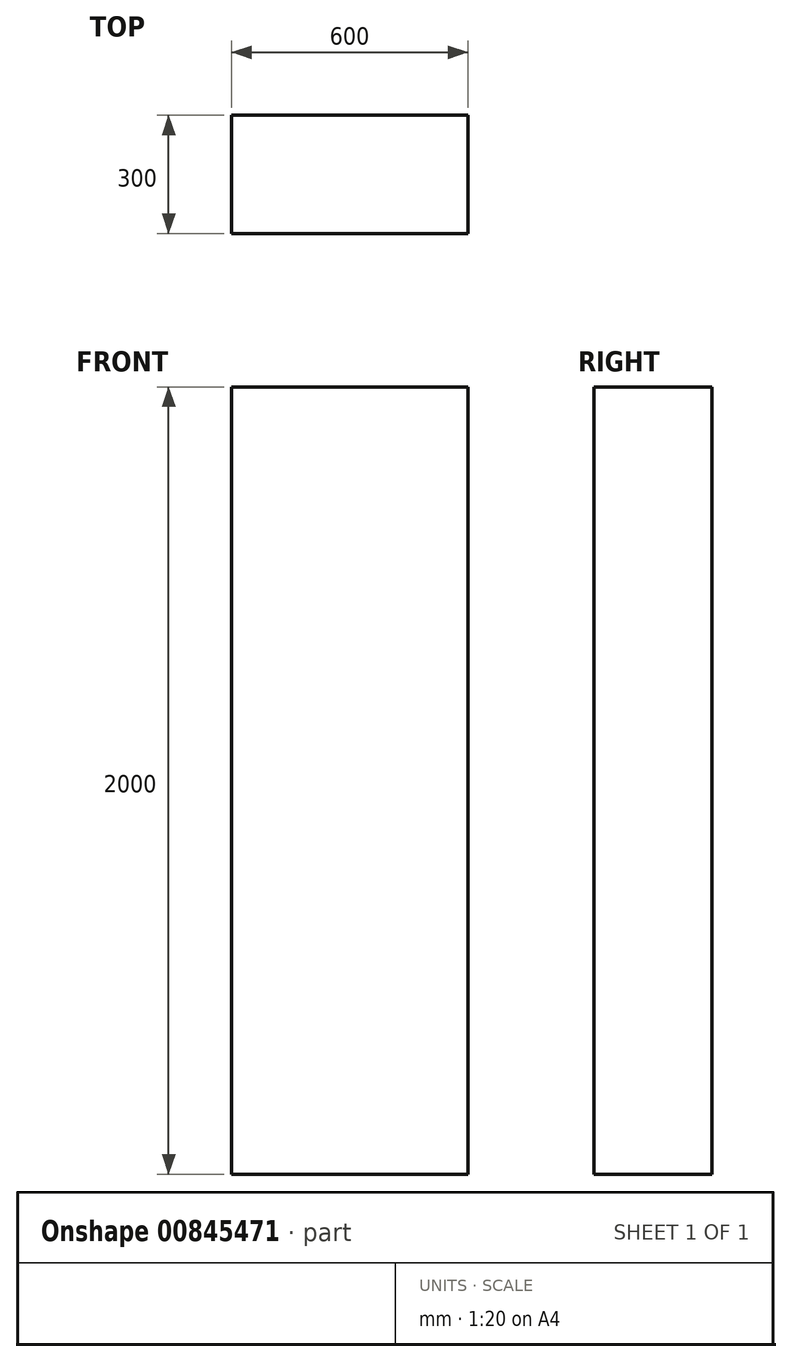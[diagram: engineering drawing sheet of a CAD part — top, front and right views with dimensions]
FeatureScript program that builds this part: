
annotation { "Feature Type Name" : "Feature", "Feature Type Description" : "" }
export const myFeature = defineFeature(function(context is Context, id is Id, definition is map)
    precondition{}
    {
        {
            var Q0;
            Q0=qCreatedBy(makeId("Top.planeOp"),FACE);
            var sketch = newSketch(context, id + "F0", { "sketchPlane" : qUnion([Q0])});
            skLineSegment(sketch, "E0.bottom", {"start": v(300, -150) * mm, "end": v(-300, -150) * mm});
            skLineSegment(sketch, "E0.top", {"start": v(300, 150) * mm, "end": v(-300, 150) * mm});
            skLineSegment(sketch, "E0.left", {"start": v(300, -150) * mm, "end": v(300, 150) * mm});
            skLineSegment(sketch, "E0.right", {"start": v(-300, -150) * mm, "end": v(-300, 150) * mm});
            skPoint(sketch, "E0.middle", {"position": v(0, 0) * mm});
            skSolve(sketch);
        }
        {
            var Q0;
            Q0=makeQuery(id+"F0.imprint","IMPRINT",FACE,{"disambiguationData":[TD([[makeQuery(id+"F0.imprint","IMPRINT",EDGE,{"derivedFrom":sQuery(id+"F0.wireOp",EDGE,"E0.bottom")}),-1.0]])]});
            extrude(context, id + "F1", {"entities" : qUnion([Q0]), "depth" : 2000 * mm, "offsetDistance" : 25 * mm});
        }
    });
